# Revit family: TapSet_Shower_Nero_Serenity_Progressive_Spout
name_source: partatom
category: Plumbing Fixtures
units: mm (PartAtom-declared; Revit-internal decimal feet)

## family parameters
Always vertical = Yes
Cut with Voids When Loaded = Yes
Maintain Annotation Orientation = No
OmniClass Number = 23.31.17.00
Part Type = Normal
Room Calculation Point = No
Round Connector Dimension = Use Diameter
Shared = No
Work Plane-Based = No

## types (1)
- Please Load From Type Catalog
    Assembly Code = D2010710
    BodyMaterial = Metal_Chrome_Nero
    CW Connection = Yes
    Default Elevation = 0 mm  [stored 0 ft]
    Description = Please Load From Type Catalog
    HW Connection = Yes
    HandleMaterial = Stone_Marble_Nero_ArabescatoCorchia
    IfcExportAs = Please Load From Type Catalog
    IfcExportType = Please Load From Type Catalog
    Manufacturer = Nero
    ManufacturerOverallDepth = 230 mm  [stored 0.754593 ft]
    ManufacturerOverallHeight = 861.6 mm  [stored 2.82677 ft]
    ManufacturerOverallWidth = 315 mm  [stored 1.03346 ft]
    ManufacturerSpecCode = Please Load From Type Catalog
    ManufacturerURLProductSpecific = https://pleaseloadfromtypecatalog.com
    Model = Please Load From Type Catalog
    ModifiedIssue = 20250131 $
    SerenityHandShower = Yes
    SlimShower = No
    Type Comments = Please Load From Type Catalog
    URL = https://nerotapware.com.au
    Uniclass2015Code = Please Load From Type Catalog
    Uniclass2015Title = Please Load From Type Catalog
    Uniclass2015Version = Please Load From Type Catalog
    Vent Connection = No
    Waste Connection = No

note: [stored X ft] marks values corroborated as IEEE doubles in the binary element streams (Revit-internal decimal feet)

## geometry (parser evidence)
native form markers: Sweep x2
no freeform markers — native parametric forms only
